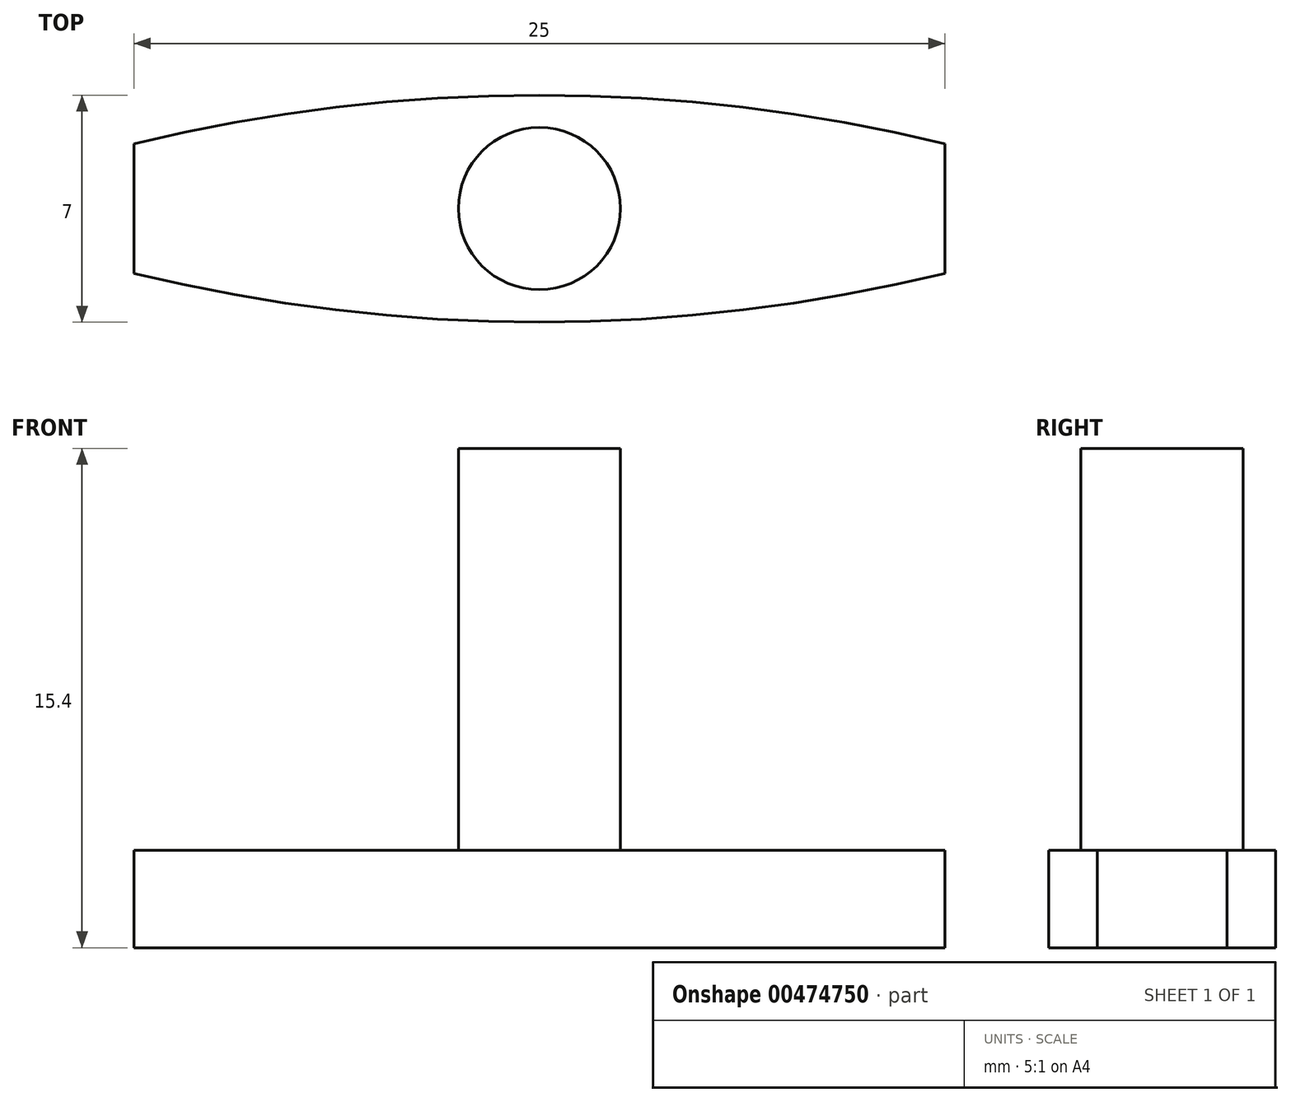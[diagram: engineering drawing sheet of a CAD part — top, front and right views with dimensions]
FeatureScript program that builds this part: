
annotation { "Feature Type Name" : "Feature", "Feature Type Description" : "" }
export const myFeature = defineFeature(function(context is Context, id is Id, definition is map)
    precondition{}
    {
        {
            var Q0;
            Q0=qCreatedBy(makeId("Top.planeOp"),FACE);
            var sketch = newSketch(context, id + "F0", { "sketchPlane" : qUnion([Q0])});
            skLineSegment(sketch, "E0.bottom", {"start": v(-12.5, 3.5) * mm, "end": v(12.5, 3.5) * mm, "construction": true});
            skLineSegment(sketch, "E0.top", {"start": v(-12.5, -3.5) * mm, "end": v(12.5, -3.5) * mm, "construction": true});
            skLineSegment(sketch, "E0.left", {"start": v(-12.5, 3.5) * mm, "end": v(-12.5, -3.5) * mm, "construction": true});
            skLineSegment(sketch, "E0.right", {"start": v(12.5, 3.5) * mm, "end": v(12.5, -3.5) * mm, "construction": true});
            skArc(sketch, "E1", {"start": v(12.5, 2) * mm, "mid": v(0, 3.5) * mm, "end": v(-12.5, 2) * mm});
            skArc(sketch, "E2", {"start": v(-12.5, -2) * mm, "mid": v(0, -3.5) * mm, "end": v(12.5, -2) * mm});
            skPoint(sketch, "E3", {"position": v(12.5, 0) * mm});
            skPoint(sketch, "E4", {"position": v(-12.5, 0) * mm});
            skLineSegment(sketch, "E5", {"start": v(-12.5, 2) * mm, "end": v(-12.5, -2) * mm});
            skLineSegment(sketch, "E6", {"start": v(12.5, 2) * mm, "end": v(12.5, -2) * mm});
            skSolve(sketch);
        }
        {
            var Q0;
            Q0 = qSketchRegion(id + "F0", true);
            extrude(context, id + "F1", {"entities" : qUnion([Q0]), "depth" : 3 * mm});
        }
        {
            var Q0;
            Q0=makeQuery(id+"F1.opExtrude","CAP_FACE",FACE,{"disambiguationData":[OSD([sQuery(id+"F0.wireOp",EDGE,"E1"),sQuery(id+"F0.wireOp",EDGE,"E2"),sQuery(id+"F0.wireOp",EDGE,"E5"),sQuery(id+"F0.wireOp",EDGE,"E6")])],"isStart":false});
            var sketch = newSketch(context, id + "F2", { "sketchPlane" : qUnion([Q0])});
            skCircle(sketch, "E7", {"center": v(0, 0) * mm, "radius": 2.5 * mm});
            skSolve(sketch);
        }
        {
            var Q0;
            Q0 = qSketchRegion(id + "F2", true);
            extrude(context, id + "F3", {"entities" : qUnion([Q0]), "operationType" : NewBodyOperationType.ADD, "depth" : 12.4 * mm});
        }
    });
